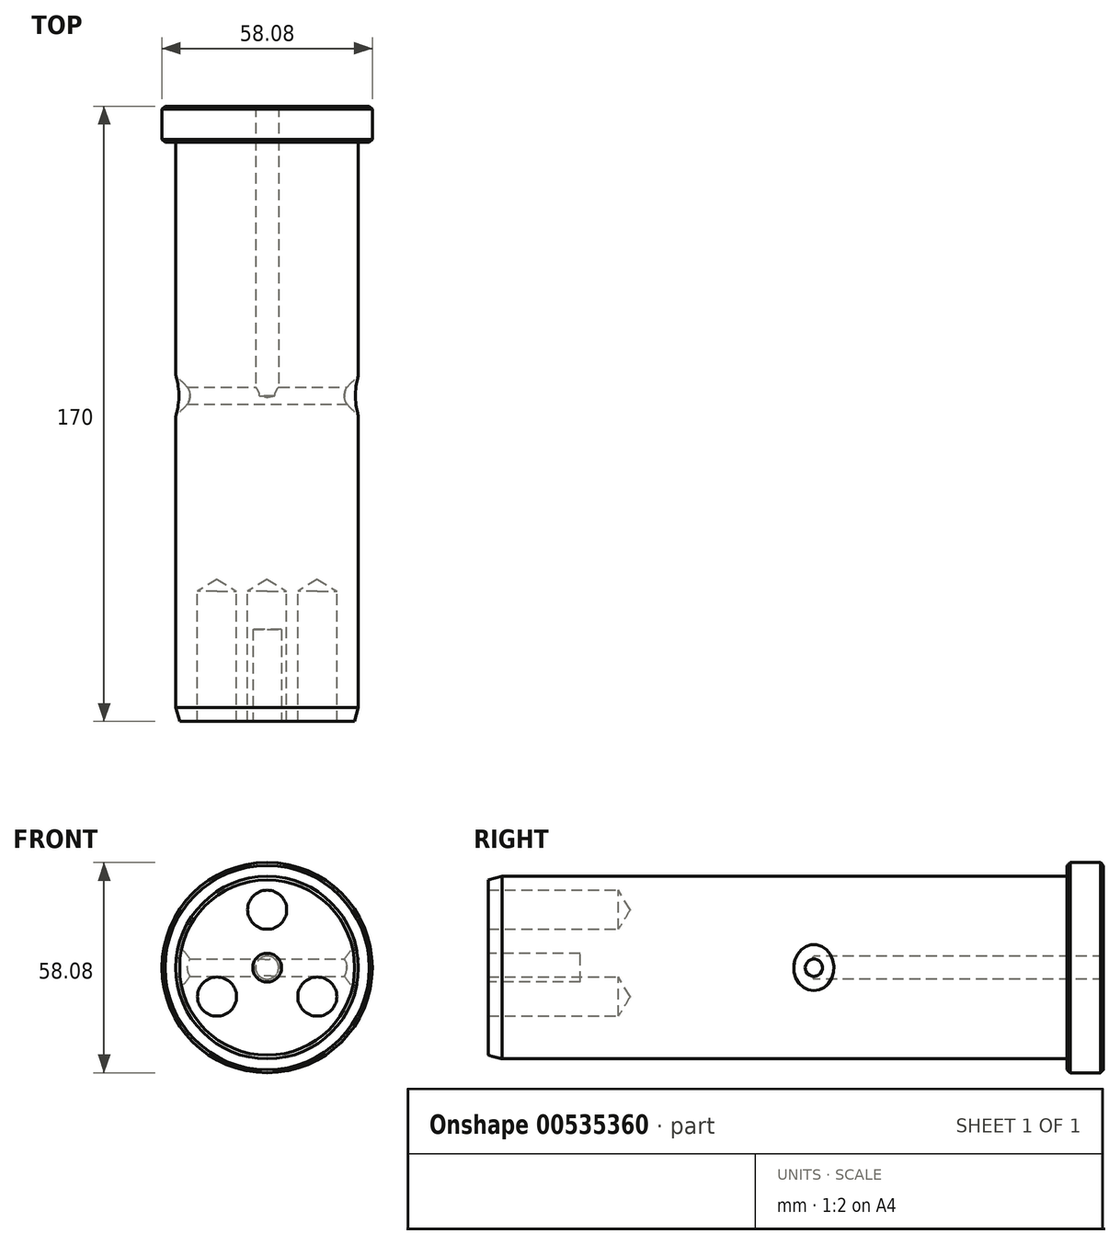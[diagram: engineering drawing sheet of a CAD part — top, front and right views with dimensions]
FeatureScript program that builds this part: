
annotation { "Feature Type Name" : "Feature", "Feature Type Description" : "" }
export const myFeature = defineFeature(function(context is Context, id is Id, definition is map)
    precondition{}
    {
        {
            var Q0;
            Q0=qCreatedBy(makeId("Front.planeOp"),FACE);
            var sketch = newSketch(context, id + "F0", { "sketchPlane" : qUnion([Q0])});
            skCircle(sketch, "E0", {"center": v(0, 0) * mm, "radius": 25.2 * mm});
            skSolve(sketch);
        }
        {
            var Q0;
            Q0=qSketchRegion(id+"F0",true);
            extrude(context, id + "F1", {"entities" : qUnion([Q0]), "depth" : 170 * mm, "offsetDistance" : 25.4 * mm});
        }
        {
            var Q0;
            Q0=makeQuery(id+"F1.opExtrude","CAP_EDGE",EDGE,{"disambiguationData":[OSD([sQuery(id+"F0.wireOp",EDGE,"E0")])],"isStart":false});
            var Q1;
            Q1=makeQuery(id+"F1.opExtrude","CAP_EDGE",EDGE,{"disambiguationData":[OSD([sQuery(id+"F0.wireOp",EDGE,"E0")])],"isStart":true});
            chamfer(context, id + "F2", {"entities" : qUnion([Q0, Q1]), "chamferType" : ChamferType.OFFSET_ANGLE, "width" : 3.8 * mm, "oppositeDirection" : true, "angle" : 15 * degree, "tangentPropagation" : true});
        }
        {
            var Q0;
            Q0=makeQuery(id+"F1.opExtrude","CAP_FACE",FACE,{"disambiguationData":[OSD([sQuery(id+"F0.wireOp",EDGE,"E0")])],"isStart":true});
            var sketch = newSketch(context, id + "F3", { "sketchPlane" : qUnion([Q0])});
            skCircle(sketch, "E1", {"center": v(0, 0) * mm, "radius": 29.04 * mm});
            skSolve(sketch);
        }
        {
            var Q0;
            Q0 = qSketchRegion(id + "F3", true);
            extrude(context, id + "F4", {"entities" : qUnion([Q0]), "operationType" : NewBodyOperationType.ADD, "oppositeDirection" : true, "depth" : 10 * mm, "offsetDistance" : 25.4 * mm});
        }
        {
            var Q0;
            Q0=makeQuery(id+"F4.boolean.opBoolean","MERGE",FACE,{"derivedFrom":[makeQuery(id+"F1.opExtrude","CAP_FACE",FACE,{"disambiguationData":[OSD([sQuery(id+"F0.wireOp",EDGE,"E0")])],"isStart":true}),makeQuery(id+"F4.opExtrude","CAP_FACE",FACE,{"disambiguationData":[OSD([sQuery(id+"F3.wireOp",EDGE,"E1")])],"isStart":true})]});
            var sketch = newSketch(context, id + "F5", { "sketchPlane" : qUnion([Q0])});
            skPoint(sketch, "E2", {"position": v(0, 0) * mm});
            skSolve(sketch);
        }
        {
            var Q0;
            Q0=sQuery(id+"F5.wireOp",VERTEX,"E2");
            var Q1;
            Q1=makeQuery(id+"F1.opExtrude","SWEPT_BODY",BODY,{"disambiguationData":[OSD([sQuery(id+"F0.wireOp",EDGE,"E0")])]});
            hole(context, id + "F6", {"style" : HoleStyle.SIMPLE, "endStyle" : HoleEndStyle.BLIND, "holeDiameter" : 6.35 * mm, "holeDepth" : 80 * mm, "isTappedThrough" : true, "tappedDepth" : 12.7 * mm, "tapClearance" : 3, "startFromSketch" : true, "locations" : qUnion([Q0]), "scope" : qUnion([Q1])});
        }
        {
            var Q0;
            Q0=qCreatedBy(makeId("Right.planeOp"),FACE);
            var sketch = newSketch(context, id + "F7", { "sketchPlane" : qUnion([Q0])});
            skCircle(sketch, "E3", {"center": v(-80, 0) * mm, "radius": 2.38 * mm});
            skSolve(sketch);
        }
        {
            var Q0;
            Q0 = qSketchRegion(id + "F7", true);
            extrude(context, id + "F8", {"entities" : qUnion([Q0]), "operationType" : NewBodyOperationType.REMOVE, "endBound" : BoundingType.THROUGH_ALL, "oppositeDirection" : true, "depth" : 25.4 * mm, "offsetDistance" : 25.4 * mm, "hasSecondDirection" : true, "secondDirectionBound" : BoundingType.THROUGH_ALL, "secondDirectionOppositeDirection" : false, "secondDirectionDepth" : 25.4 * mm});
        }
        {
            var Q0;
            Q0=makeQuery(id+"F8.boolean.opBoolean","INTERSECT",EDGE,{"disambiguationData":[OD(1.0)],"derivedFrom":[makeQuery(id+"F1.opExtrude","SWEPT_FACE",FACE,{"disambiguationData":[OSD([sQuery(id+"F0.wireOp",EDGE,"E0")])]}),makeQuery(id+"F8.opExtrude","SWEPT_FACE",FACE,{"disambiguationData":[OSD([sQuery(id+"F7.wireOp",EDGE,"E3")])]})]});
            var Q1;
            Q1=makeQuery(id+"F8.boolean.opBoolean","INTERSECT",EDGE,{"disambiguationData":[OD(0.0)],"derivedFrom":[makeQuery(id+"F1.opExtrude","SWEPT_FACE",FACE,{"disambiguationData":[OSD([sQuery(id+"F0.wireOp",EDGE,"E0")])]}),makeQuery(id+"F8.opExtrude","SWEPT_FACE",FACE,{"disambiguationData":[OSD([sQuery(id+"F7.wireOp",EDGE,"E3")])]})]});
            chamfer(context, id + "F9", {"entities" : qUnion([Q0, Q1]), "width" : 3.17 * mm, "tangentPropagation" : true});
        }
        {
            var Q0;
            Q0=makeQuery(id+"F1.opExtrude","CAP_FACE",FACE,{"disambiguationData":[OSD([sQuery(id+"F0.wireOp",EDGE,"E0")])],"isStart":false});
            var sketch = newSketch(context, id + "F10", { "sketchPlane" : qUnion([Q0])});
            skCircle(sketch, "E4", {"center": v(0, 0) * mm, "radius": 16 * mm});
            skPoint(sketch, "E5", {"position": v(0, 16) * mm});
            skPoint(sketch, "E6.1.0", {"position": v(-13.86, -8) * mm});
            skPoint(sketch, "E6.2.0", {"position": v(13.86, -8) * mm});
            skSolve(sketch);
        }
        {
            var Q0;
            Q0=sQuery(id+"F10.wireOp",VERTEX,"E5");
            var Q1;
            Q1=sQuery(id+"F10.wireOp",VERTEX,"E6.1.0");
            var Q2;
            Q2=sQuery(id+"F10.wireOp",VERTEX,"E6.2.0");
            var Q3;
            Q3=makeQuery(id+"F1.opExtrude","SWEPT_BODY",BODY,{"disambiguationData":[OSD([sQuery(id+"F0.wireOp",EDGE,"E0")])]});
            hole(context, id + "F11", {"style" : HoleStyle.SIMPLE, "endStyle" : HoleEndStyle.BLIND, "holeDiameter" : 10.8 * mm, "holeDepth" : 36 * mm, "isTappedThrough" : true, "tappedDepth" : 12.7 * mm, "tapClearance" : 3, "startFromSketch" : true, "locations" : qUnion([Q0, Q1, Q2]), "scope" : qUnion([Q3])});
        }
        {
            var Q0;
            Q0=makeQuery(id+"F4.opExtrude","SWEPT_FACE",FACE,{"disambiguationData":[OSD([sQuery(id+"F3.wireOp",EDGE,"E1")])]});
            chamfer(context, id + "F12", {"entities" : qUnion([Q0]), "width" : 0.81 * mm, "tangentPropagation" : true});
        }
        {
            var Q0;
            Q0=makeQuery(id+"F1.opExtrude","CAP_FACE",FACE,{"disambiguationData":[OSD([sQuery(id+"F0.wireOp",EDGE,"E0")])],"isStart":false});
            var sketch = newSketch(context, id + "F13", { "sketchPlane" : qUnion([Q0])});
            skCircle(sketch, "E7", {"center": v(0, 0) * mm, "radius": 3.97 * mm});
            skSolve(sketch);
        }
        {
            var Q0;
            Q0 = qSketchRegion(id + "F13", true);
            extrude(context, id + "F14", {"entities" : qUnion([Q0]), "operationType" : NewBodyOperationType.REMOVE, "oppositeDirection" : true, "depth" : 25.4 * mm, "offsetDistance" : 25.4 * mm});
        }
    });
